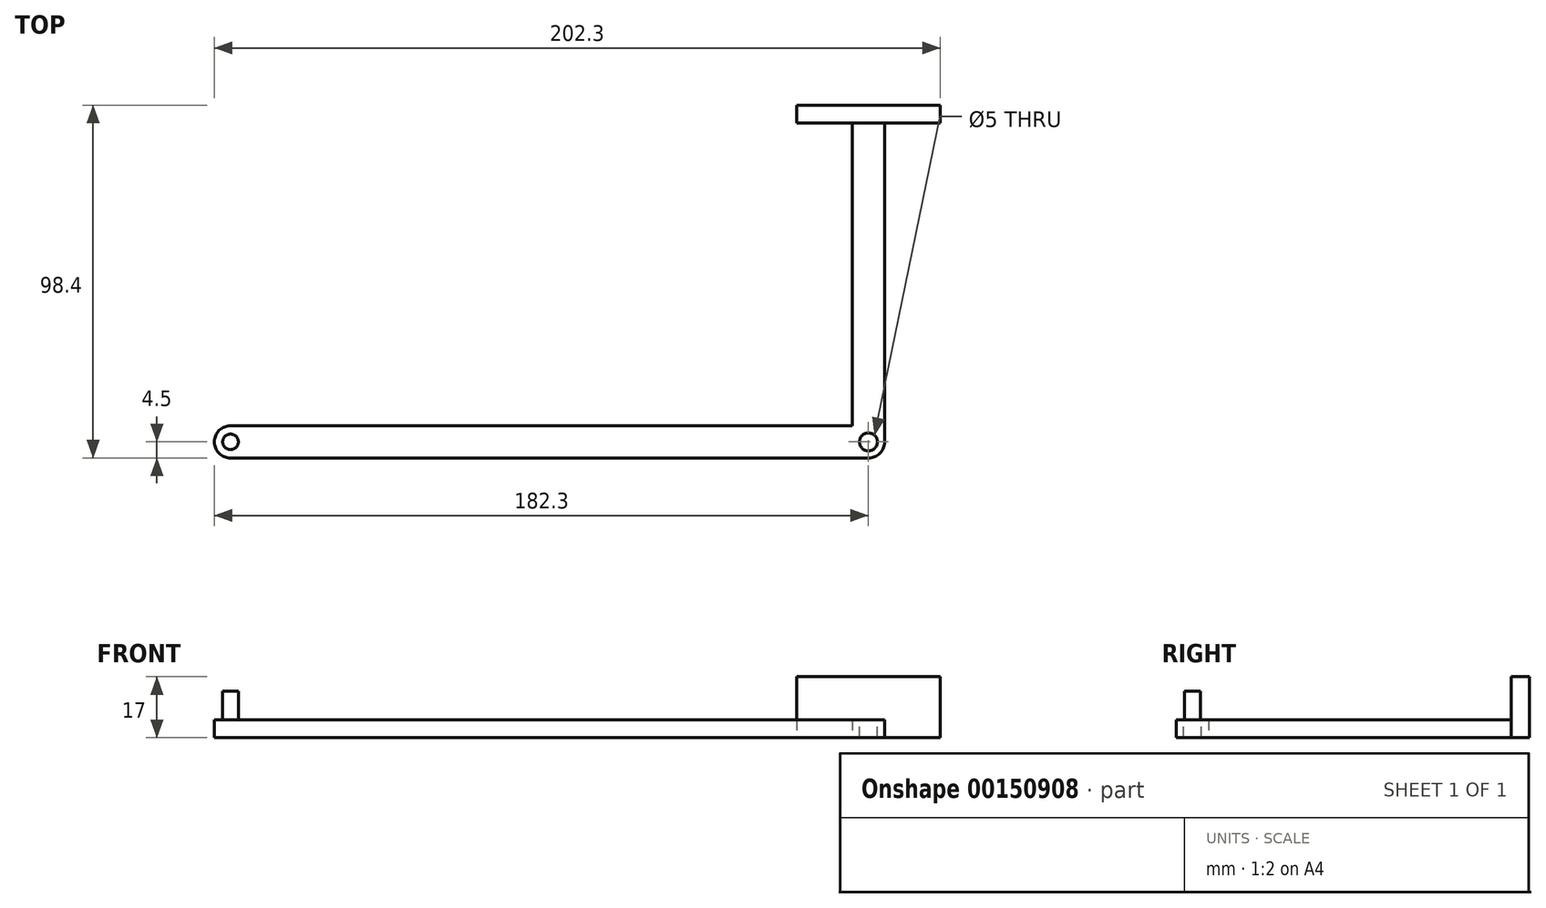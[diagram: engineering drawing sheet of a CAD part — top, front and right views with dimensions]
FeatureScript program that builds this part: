
annotation { "Feature Type Name" : "Feature", "Feature Type Description" : "" }
export const myFeature = defineFeature(function(context is Context, id is Id, definition is map)
    precondition{}
    {
        {
            var Q0;
            Q0=qCreatedBy(makeId("Top.planeOp"),FACE);
            var sketch = newSketch(context, id + "F0", { "sketchPlane" : qUnion([Q0])});
            skLineSegment(sketch, "E0", {"start": v(-24.5, 98.4) * mm, "end": v(15.5, 98.4) * mm});
            skLineSegment(sketch, "E1", {"start": v(15.5, 98.4) * mm, "end": v(15.5, 93.4) * mm});
            skLineSegment(sketch, "E2", {"start": v(15.5, 93.4) * mm, "end": v(0, 93.4) * mm});
            skLineSegment(sketch, "E3", {"start": v(0, 93.4) * mm, "end": v(0, 4.5) * mm});
            skLineSegment(sketch, "E4", {"start": v(-4.5, 0) * mm, "end": v(-182.3, 0) * mm});
            skLineSegment(sketch, "E5", {"start": v(-182.3, 9) * mm, "end": v(-9, 9) * mm});
            skLineSegment(sketch, "E6", {"start": v(-9, 9) * mm, "end": v(-9, 93.4) * mm});
            skLineSegment(sketch, "E7", {"start": v(-9, 93.4) * mm, "end": v(-24.5, 93.4) * mm});
            skLineSegment(sketch, "E8", {"start": v(-24.5, 93.4) * mm, "end": v(-24.5, 98.4) * mm});
            skArc(sketch, "E9", {"start": v(-4.5, 0) * mm, "mid": v(-1.32, 1.32) * mm, "end": v(0, 4.5) * mm});
            skArc(sketch, "E10", {"start": v(-182.3, 9) * mm, "mid": v(-186.8, 4.5) * mm, "end": v(-182.3, 0) * mm});
            skSolve(sketch);
        }
        {
            var Q0;
            Q0 = qSketchRegion(id + "F0", true);
            extrude(context, id + "F1", {"entities" : qUnion([Q0]), "depth" : 5 * mm});
        }
        {
            var Q0;
            Q0=makeQuery(id+"F1.opExtrude","CAP_FACE",FACE,{"disambiguationData":[OSD([sQuery(id+"F0.wireOp",EDGE,"E0"),sQuery(id+"F0.wireOp",EDGE,"E1"),sQuery(id+"F0.wireOp",EDGE,"E2"),sQuery(id+"F0.wireOp",EDGE,"E3"),sQuery(id+"F0.wireOp",EDGE,"E4"),sQuery(id+"F0.wireOp",EDGE,"E5"),sQuery(id+"F0.wireOp",EDGE,"E6"),sQuery(id+"F0.wireOp",EDGE,"E7"),sQuery(id+"F0.wireOp",EDGE,"E8"),sQuery(id+"F0.wireOp",EDGE,"E9"),sQuery(id+"F0.wireOp",EDGE,"E10")])],"isStart":false});
            var sketch = newSketch(context, id + "F2", { "sketchPlane" : qUnion([Q0])});
            skLineSegment(sketch, "E11.bottom", {"start": v(-24.5, 98.4) * mm, "end": v(15.5, 98.4) * mm});
            skLineSegment(sketch, "E11.top", {"start": v(-24.5, 93.4) * mm, "end": v(15.5, 93.4) * mm});
            skLineSegment(sketch, "E11.left", {"start": v(-24.5, 98.4) * mm, "end": v(-24.5, 93.4) * mm});
            skLineSegment(sketch, "E11.right", {"start": v(15.5, 98.4) * mm, "end": v(15.5, 93.4) * mm});
            skSolve(sketch);
        }
        {
            var Q0;
            Q0 = qSketchRegion(id + "F2", true);
            extrude(context, id + "F3", {"entities" : qUnion([Q0]), "operationType" : NewBodyOperationType.ADD, "depth" : 12 * mm});
        }
        {
            var Q0;
            Q0=makeQuery(id+"F1.opExtrude","CAP_FACE",FACE,{"disambiguationData":[OSD([sQuery(id+"F0.wireOp",EDGE,"E0"),sQuery(id+"F0.wireOp",EDGE,"E1"),sQuery(id+"F0.wireOp",EDGE,"E2"),sQuery(id+"F0.wireOp",EDGE,"E3"),sQuery(id+"F0.wireOp",EDGE,"E4"),sQuery(id+"F0.wireOp",EDGE,"E5"),sQuery(id+"F0.wireOp",EDGE,"E6"),sQuery(id+"F0.wireOp",EDGE,"E7"),sQuery(id+"F0.wireOp",EDGE,"E8"),sQuery(id+"F0.wireOp",EDGE,"E9"),sQuery(id+"F0.wireOp",EDGE,"E10")])],"isStart":false});
            var sketch = newSketch(context, id + "F4", { "sketchPlane" : qUnion([Q0])});
            skCircle(sketch, "E12", {"center": v(-182.3, 4.5) * mm, "radius": 2.18 * mm});
            skSolve(sketch);
        }
        {
            var Q0;
            Q0 = qSketchRegion(id + "F4", true);
            extrude(context, id + "F5", {"entities" : qUnion([Q0]), "operationType" : NewBodyOperationType.ADD, "depth" : 8 * mm});
        }
        {
            var Q0;
            Q0=makeQuery(id+"F1.opExtrude","CAP_FACE",FACE,{"disambiguationData":[OSD([sQuery(id+"F0.wireOp",EDGE,"E0"),sQuery(id+"F0.wireOp",EDGE,"E1"),sQuery(id+"F0.wireOp",EDGE,"E2"),sQuery(id+"F0.wireOp",EDGE,"E3"),sQuery(id+"F0.wireOp",EDGE,"E4"),sQuery(id+"F0.wireOp",EDGE,"E5"),sQuery(id+"F0.wireOp",EDGE,"E6"),sQuery(id+"F0.wireOp",EDGE,"E7"),sQuery(id+"F0.wireOp",EDGE,"E8"),sQuery(id+"F0.wireOp",EDGE,"E9"),sQuery(id+"F0.wireOp",EDGE,"E10")])],"isStart":false});
            var sketch = newSketch(context, id + "F6", { "sketchPlane" : qUnion([Q0])});
            skCircle(sketch, "E13", {"center": v(-4.5, 4.5) * mm, "radius": 2.5 * mm});
            skSolve(sketch);
        }
        {
            var Q0;
            Q0 = qSketchRegion(id + "F6", true);
            extrude(context, id + "F7", {"entities" : qUnion([Q0]), "operationType" : NewBodyOperationType.REMOVE, "oppositeDirection" : true, "depth" : 25 * mm});
        }
    });
